# Revit family: Traverse
name_source: partatom
category: Lighting Fixtures
revit_build: Autodesk Revit Architecture 2012 (Build: 20110309_2315(x64)
units: mm (PartAtom-declared; Revit-internal decimal feet)

## types (12) — shared parameters
Apparent Load = 0 VA
Color Filter = 16777215
Default Elevation = 48"
Description = This totally new designed LED WALLPACK has been created to optimize the LED source with its lighting performance and thermal management.
Dimming Lamp Color Temperature Shift = <None>
Emit Shape Visible in Rendering = No
Emit from Rectangle Length = 9"
Emit from Rectangle Width = 10"
Glass = White Glass
Lamp = LED Lamp
Load Classification = Lighting
Manufacturer = Beacon Lighting
Manufacturer Fax = (941) 751-5535
Model = TRAVERSE
Nominal Watts = 27 W
Photometric Link = http://www.beaconproducts.com
Photometric Web File = TRV-24NB-55-3K-T2.ies
Product Documentation Link = http://www.beaconproducts.com
Product Page URL = http://www.beaconproducts.com
Tilt Angle = 90.00°
URL = http://www.beaconproducts.com
Voltage = 120 V
Wattage Comments = 27W to 136W

## per-type parameters (varying)
| type | Backbox |
| TRV-BBT | Black Textured |
| TRV-BMT | Black Matte Textured |
| TRV-WHT | White |
| TRV-BZT | Bronze Textured |
| TRV-MBT | Mettalic Bronze Textured |
| TRV-DBT | Dark  Bronze Textured |
| TRV-GYS | Grey smooth |
| TRV-DPS | Dark Platinum Smooth |
| TRV-GNT | <By Category> |
| TRV-MST | Mettallic Silver Textured |
| TRV-MTT | Metallic titanium textured |
| TRV-OWI | Old World Iron |

## geometry (parser evidence)
native form markers: Blend x13, Sweep x2
no freeform markers — native parametric forms only
